# Revit family: LIO-Wall
name_source: partatom
category: Lighting Fixtures
units: mm (PartAtom-declared; Revit-internal decimal feet)

## family parameters
Always vertical = Yes
Cut with Voids When Loaded = No
Host = Wall
Light Source = No
OmniClass Number = 23.80.70.00
OmniClass Title = Lighting
Part Type = Normal
Room Calculation Point = No
Round Connector Dimension = Use Diameter
Shared = No

## types (3) — shared parameters
Bulb Diametr = 15 mm  [stored 0.0492126 ft]
Description = WALL LAMP
Designer = Studio Debonademeo
Manufacturer = Vistosi
Manufacturer country = Italy
Model = LIO
Type Comments = Studio Debonademeo
URL = https://vistosi.com
URL Product Page = https://vistosi.it
zero-valued in all types: Default Elevation

## per-type parameters (varying)
| type | Depth | Lampshade Type | Width |
| LIO AP 30 | 0 mm  [stored 0 ft] | LIO_Lampshade : LIO PL 30 | 18 mm |
| LIO AP 40 | 0 mm  [stored 0 ft] | LIO_Lampshade : LIO PL 40 | 18 mm |
| LIO AP 50 | 12 mm  [stored 0.0393701 ft] | LIO_Lampshade : LIO PL 50 | 8 mm  [stored 0.0262467 ft] |

note: [stored X ft] marks values corroborated as IEEE doubles in the binary element streams (Revit-internal decimal feet)

## geometry (parser evidence)
native form markers: Sweep x5
no freeform markers — native parametric forms only
